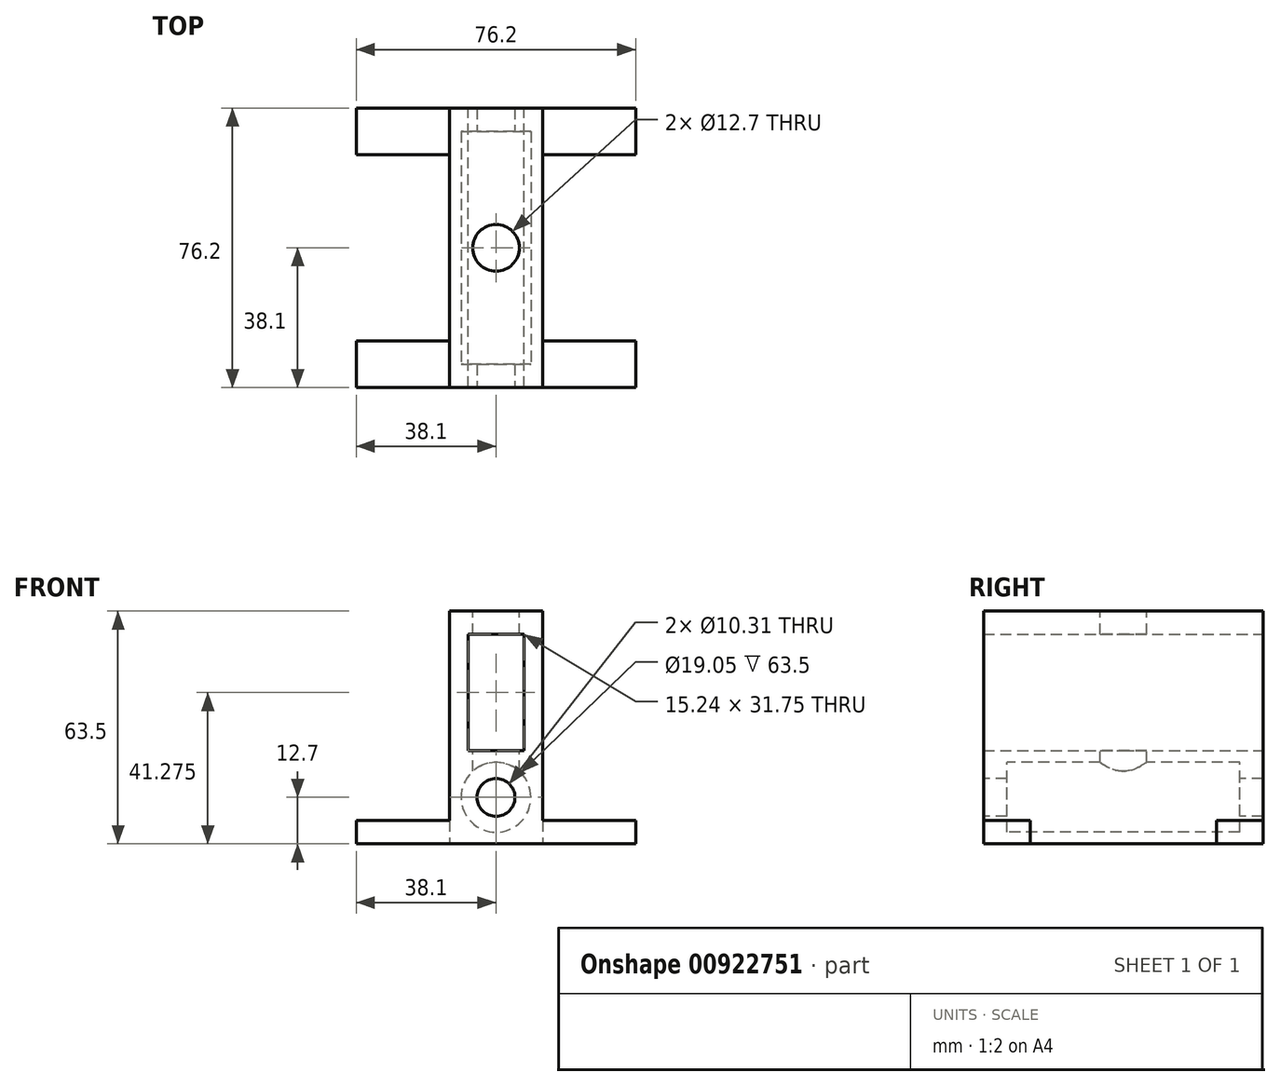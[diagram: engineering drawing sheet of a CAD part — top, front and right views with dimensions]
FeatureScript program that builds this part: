
annotation { "Feature Type Name" : "Feature", "Feature Type Description" : "" }
export const myFeature = defineFeature(function(context is Context, id is Id, definition is map)
    precondition{}
    {
        {
            var Q0;
            Q0=qCreatedBy(makeId("Top.planeOp"),FACE);
            var sketch = newSketch(context, id + "F0", { "sketchPlane" : qUnion([Q0])});
            skLineSegment(sketch, "E0.bottom", {"start": v(0, 0) * mm, "end": v(25.4, 0) * mm});
            skLineSegment(sketch, "E0.top", {"start": v(0, 76.2) * mm, "end": v(25.4, 76.2) * mm});
            skLineSegment(sketch, "E0.left", {"start": v(0, 0) * mm, "end": v(0, 76.2) * mm});
            skLineSegment(sketch, "E0.right", {"start": v(25.4, 0) * mm, "end": v(25.4, 76.2) * mm});
            skSolve(sketch);
        }
        {
            var Q0;
            Q0=makeQuery(id+"F0.imprint","IMPRINT",FACE,{"disambiguationData":[TD([[makeQuery(id+"F0.imprint","IMPRINT",EDGE,{"derivedFrom":sQuery(id+"F0.wireOp",EDGE,"E0.bottom")}),1.0]])]});
            extrude(context, id + "F1", {"entities" : qUnion([Q0]), "depth" : 25.4 * mm, "offsetDistance" : 25.4 * mm});
        }
        {
            var Q0;
            Q0=qCreatedBy(makeId("Top.planeOp"),FACE);
            var sketch = newSketch(context, id + "F2", { "sketchPlane" : qUnion([Q0])});
            skLineSegment(sketch, "E1.bottom", {"start": v(25.4, 0) * mm, "end": v(50.8, 0) * mm});
            skLineSegment(sketch, "E1.top", {"start": v(25.4, 12.7) * mm, "end": v(50.8, 12.7) * mm});
            skLineSegment(sketch, "E1.left", {"start": v(25.4, 0) * mm, "end": v(25.4, 12.7) * mm});
            skLineSegment(sketch, "E1.right", {"start": v(50.8, 0) * mm, "end": v(50.8, 12.7) * mm});
            skLineSegment(sketch, "E2.bottom", {"start": v(0, 0) * mm, "end": v(-25.4, 0) * mm});
            skLineSegment(sketch, "E2.top", {"start": v(0, 12.7) * mm, "end": v(-25.4, 12.7) * mm});
            skLineSegment(sketch, "E2.left", {"start": v(0, 0) * mm, "end": v(0, 12.7) * mm});
            skLineSegment(sketch, "E2.right", {"start": v(-25.4, 0) * mm, "end": v(-25.4, 12.7) * mm});
            skLineSegment(sketch, "E3.bottom", {"start": v(0, 76.2) * mm, "end": v(-25.4, 76.2) * mm});
            skLineSegment(sketch, "E3.top", {"start": v(0, 63.5) * mm, "end": v(-25.4, 63.5) * mm});
            skLineSegment(sketch, "E3.left", {"start": v(0, 76.2) * mm, "end": v(0, 63.5) * mm});
            skLineSegment(sketch, "E3.right", {"start": v(-25.4, 76.2) * mm, "end": v(-25.4, 63.5) * mm});
            skLineSegment(sketch, "E4.bottom", {"start": v(25.4, 76.2) * mm, "end": v(50.8, 76.2) * mm});
            skLineSegment(sketch, "E4.top", {"start": v(25.4, 63.5) * mm, "end": v(50.8, 63.5) * mm});
            skLineSegment(sketch, "E4.left", {"start": v(25.4, 76.2) * mm, "end": v(25.4, 63.5) * mm});
            skLineSegment(sketch, "E4.right", {"start": v(50.8, 76.2) * mm, "end": v(50.8, 63.5) * mm});
            skSolve(sketch);
        }
        {
            var Q0;
            Q0=makeQuery(id+"F2.imprint","IMPRINT",FACE,{"disambiguationData":[TD([[makeQuery(id+"F2.imprint","IMPRINT",EDGE,{"derivedFrom":sQuery(id+"F2.wireOp",EDGE,"E2.bottom")}),-1.0]])]});
            var Q1;
            Q1=makeQuery(id+"F2.imprint","IMPRINT",FACE,{"disambiguationData":[TD([[makeQuery(id+"F2.imprint","IMPRINT",EDGE,{"derivedFrom":sQuery(id+"F2.wireOp",EDGE,"E1.bottom")}),1.0]])]});
            var Q2;
            Q2=makeQuery(id+"F2.imprint","IMPRINT",FACE,{"disambiguationData":[TD([[makeQuery(id+"F2.imprint","IMPRINT",EDGE,{"derivedFrom":sQuery(id+"F2.wireOp",EDGE,"E3.bottom")}),1.0]])]});
            var Q3;
            Q3=makeQuery(id+"F2.imprint","IMPRINT",FACE,{"disambiguationData":[TD([[makeQuery(id+"F2.imprint","IMPRINT",EDGE,{"derivedFrom":sQuery(id+"F2.wireOp",EDGE,"E4.bottom")}),-1.0]])]});
            extrude(context, id + "F3", {"entities" : qUnion([Q0, Q1, Q2, Q3]), "operationType" : NewBodyOperationType.ADD, "depth" : 6.35 * mm, "offsetDistance" : 25.4 * mm});
        }
        {
            var Q0;
            Q0=makeQuery(id+"F3.boolean.opBoolean","MERGE",FACE,{"derivedFrom":[makeQuery(id+"F1.opExtrude","SWEPT_FACE",FACE,{"disambiguationData":[OSD([sQuery(id+"F0.wireOp",EDGE,"E0.bottom")])]}),makeQuery(id+"F3.opExtrude","SWEPT_FACE",FACE,{"disambiguationData":[OSD([sQuery(id+"F2.wireOp",EDGE,"E1.bottom")])]}),makeQuery(id+"F3.opExtrude","SWEPT_FACE",FACE,{"disambiguationData":[OSD([sQuery(id+"F2.wireOp",EDGE,"E2.bottom")])]})]});
            var sketch = newSketch(context, id + "F4", { "sketchPlane" : qUnion([Q0])});
            skCircle(sketch, "E5", {"center": v(12.7, 12.7) * mm, "radius": 9.53 * mm});
            skSolve(sketch);
        }
        {
            var Q0;
            Q0=makeQuery(id+"F4.imprint","IMPRINT",FACE,{"disambiguationData":[TD([[makeQuery(id+"F4.imprint","IMPRINT",EDGE,{"derivedFrom":sQuery(id+"F4.wireOp",EDGE,"E5")}),1.0]])]});
            var Q1;
            Q1=sQuery(id+"F4.wireOp",EDGE,"E5");
            extrude(context, id + "F5", {"entities" : qUnion([Q0]), "operationType" : NewBodyOperationType.REMOVE, "surfaceEntities" : qUnion([Q1]), "oppositeDirection" : true, "depth" : 69.85 * mm, "offsetDistance" : 25.4 * mm, "hasSecondDirection" : true, "secondDirectionOppositeDirection" : false, "secondDirectionDepth" : -6.35 * mm});
        }
        {
            var Q0;
            Q0=makeQuery(id+"F3.boolean.opBoolean","MERGE",FACE,{"derivedFrom":[makeQuery(id+"F1.opExtrude","SWEPT_FACE",FACE,{"disambiguationData":[OSD([sQuery(id+"F0.wireOp",EDGE,"E0.bottom")])]}),makeQuery(id+"F3.opExtrude","SWEPT_FACE",FACE,{"disambiguationData":[OSD([sQuery(id+"F2.wireOp",EDGE,"E1.bottom")])]}),makeQuery(id+"F3.opExtrude","SWEPT_FACE",FACE,{"disambiguationData":[OSD([sQuery(id+"F2.wireOp",EDGE,"E2.bottom")])]})]});
            var sketch = newSketch(context, id + "F6", { "sketchPlane" : qUnion([Q0])});
            skCircle(sketch, "E6", {"center": v(12.7, 12.7) * mm, "radius": 5.16 * mm});
            skSolve(sketch);
        }
        {
            var Q0;
            Q0=makeQuery(id+"F6.imprint","IMPRINT",FACE,{"disambiguationData":[TD([[makeQuery(id+"F6.imprint","IMPRINT",EDGE,{"derivedFrom":sQuery(id+"F6.wireOp",EDGE,"E6")}),1.0]])]});
            extrude(context, id + "F7", {"entities" : qUnion([Q0]), "operationType" : NewBodyOperationType.REMOVE, "endBound" : BoundingType.THROUGH_ALL, "oppositeDirection" : true, "depth" : 25.4 * mm, "offsetDistance" : 25.4 * mm});
        }
        {
            var Q0;
            Q0=makeQuery(id+"F1.opExtrude","CAP_FACE",FACE,{"disambiguationData":[OSD([sQuery(id+"F0.wireOp",EDGE,"E0.bottom"),sQuery(id+"F0.wireOp",EDGE,"E0.top"),sQuery(id+"F0.wireOp",EDGE,"E0.left"),sQuery(id+"F0.wireOp",EDGE,"E0.right")])],"isStart":false});
            var sketch = newSketch(context, id + "F8", { "sketchPlane" : qUnion([Q0])});
            skCircle(sketch, "E7", {"center": v(12.7, 12.7) * mm, "radius": 6.35 * mm});
            skCircle(sketch, "E8", {"center": v(12.7, 38.1) * mm, "radius": 6.35 * mm});
            skCircle(sketch, "E9", {"center": v(12.7, 63.5) * mm, "radius": 6.35 * mm});
            skSolve(sketch);
        }
        {
            var Q0;
            Q0=makeQuery(id+"F1.opExtrude","CAP_FACE",FACE,{"disambiguationData":[OSD([sQuery(id+"F0.wireOp",EDGE,"E0.bottom"),sQuery(id+"F0.wireOp",EDGE,"E0.top"),sQuery(id+"F0.wireOp",EDGE,"E0.left"),sQuery(id+"F0.wireOp",EDGE,"E0.right")])],"isStart":false});
            var sketch = newSketch(context, id + "F9", { "sketchPlane" : qUnion([Q0])});
            skLineSegment(sketch, "E10.bottom", {"start": v(25.4, 0) * mm, "end": v(20.32, 0) * mm});
            skLineSegment(sketch, "E10.top", {"start": v(25.4, 76.2) * mm, "end": v(20.32, 76.2) * mm});
            skLineSegment(sketch, "E10.left", {"start": v(25.4, 0) * mm, "end": v(25.4, 76.2) * mm});
            skLineSegment(sketch, "E10.right", {"start": v(20.32, 0) * mm, "end": v(20.32, 76.2) * mm});
            skLineSegment(sketch, "E11.bottom", {"start": v(0, 0) * mm, "end": v(5.08, 0) * mm});
            skLineSegment(sketch, "E11.top", {"start": v(0, 76.2) * mm, "end": v(5.08, 76.2) * mm});
            skLineSegment(sketch, "E11.left", {"start": v(0, 0) * mm, "end": v(0, 76.2) * mm});
            skLineSegment(sketch, "E11.right", {"start": v(5.08, 0) * mm, "end": v(5.08, 76.2) * mm});
            skSolve(sketch);
        }
        {
            var Q0;
            Q0=makeQuery(id+"F9.imprint","IMPRINT",FACE,{"disambiguationData":[TD([[makeQuery(id+"F9.imprint","IMPRINT",EDGE,{"derivedFrom":sQuery(id+"F9.wireOp",EDGE,"E10.bottom")}),1.0]])]});
            var Q1;
            Q1=makeQuery(id+"F9.imprint","IMPRINT",FACE,{"disambiguationData":[TD([[makeQuery(id+"F9.imprint","IMPRINT",EDGE,{"derivedFrom":sQuery(id+"F9.wireOp",EDGE,"E11.bottom")}),1.0]])]});
            extrude(context, id + "F10", {"entities" : qUnion([Q0, Q1]), "operationType" : NewBodyOperationType.ADD, "depth" : 38.1 * mm, "offsetDistance" : 25.4 * mm});
        }
        {
            var Q0;
            Q0=makeQuery(id+"F10.opExtrude","CAP_FACE",FACE,{"disambiguationData":[OSD([sQuery(id+"F9.wireOp",EDGE,"E10.bottom"),sQuery(id+"F9.wireOp",EDGE,"E10.top"),sQuery(id+"F9.wireOp",EDGE,"E10.left"),sQuery(id+"F9.wireOp",EDGE,"E10.right")])],"isStart":false});
            var sketch = newSketch(context, id + "F11", { "sketchPlane" : qUnion([Q0])});
            skLineSegment(sketch, "E12.bottom", {"start": v(25.4, 76.2) * mm, "end": v(0, 76.2) * mm});
            skLineSegment(sketch, "E12.top", {"start": v(25.4, 0) * mm, "end": v(0, 0) * mm});
            skLineSegment(sketch, "E12.left", {"start": v(25.4, 76.2) * mm, "end": v(25.4, 0) * mm});
            skLineSegment(sketch, "E12.right", {"start": v(0, 76.2) * mm, "end": v(0, 0) * mm});
            skSolve(sketch);
        }
        {
            var Q0;
            {var subQ2=sQuery(id+"F11.wireOp",EDGE,"E12.right");Q0=makeQuery(id+"F11.imprint","IMPRINT",FACE,{"disambiguationData":[TD([[makeQuery(id+"F11.imprint","IMPRINT",EDGE,{"derivedFrom":subQ2}),1.0]])]});}
            extrude(context, id + "F12", {"entities" : qUnion([Q0]), "operationType" : NewBodyOperationType.ADD, "oppositeDirection" : true, "depth" : 6.35 * mm, "offsetDistance" : 25.4 * mm});
        }
        {
            var Q0;
            Q0=makeQuery(id+"F8.imprint","IMPRINT",FACE,{"disambiguationData":[TD([[makeQuery(id+"F8.imprint","IMPRINT",EDGE,{"derivedFrom":sQuery(id+"F8.wireOp",EDGE,"E8")}),1.0]])]});
            var Q1;
            Q1=sQuery(id+"F8.wireOp",EDGE,"E7");
            extrude(context, id + "F13", {"entities" : qUnion([Q0]), "operationType" : NewBodyOperationType.REMOVE, "surfaceEntities" : qUnion([Q1]), "endBound" : BoundingType.UP_TO_NEXT, "oppositeDirection" : true, "depth" : 25.4 * mm, "offsetDistance" : 25.4 * mm, "hasSecondDirection" : true, "secondDirectionBound" : SecondDirectionBoundingType.THROUGH_ALL, "secondDirectionOppositeDirection" : false, "secondDirectionDepth" : 25.4 * mm});
        }
    });
